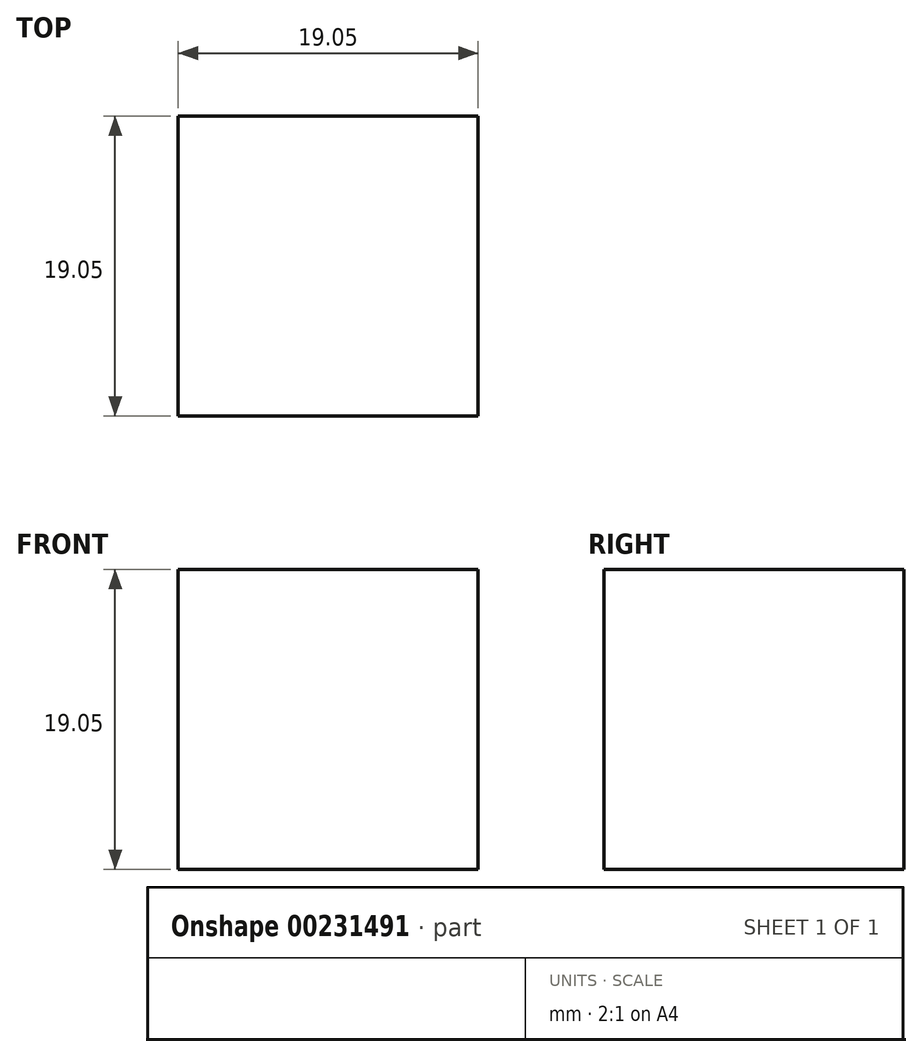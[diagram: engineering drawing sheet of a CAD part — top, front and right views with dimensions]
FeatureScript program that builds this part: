
annotation { "Feature Type Name" : "Feature", "Feature Type Description" : "" }
export const myFeature = defineFeature(function(context is Context, id is Id, definition is map)
    precondition{}
    {
        {
            var Q0;
            Q0=qCreatedBy(makeId("Front.planeOp"),FACE);
            var sketch = newSketch(context, id + "F0", { "sketchPlane" : qUnion([Q0])});
            skLineSegment(sketch, "E0.bottom", {"start": v(-64.04, 46.77) * mm, "end": v(-45, 46.77) * mm});
            skLineSegment(sketch, "E0.top", {"start": v(-64.04, 27.72) * mm, "end": v(-45, 27.72) * mm});
            skLineSegment(sketch, "E0.left", {"start": v(-64.04, 46.77) * mm, "end": v(-64.04, 27.72) * mm});
            skLineSegment(sketch, "E0.right", {"start": v(-45, 46.77) * mm, "end": v(-45, 27.72) * mm});
            skSolve(sketch);
        }
        {
            var Q0;
            Q0=makeQuery(id+"F0.imprint","IMPRINT",FACE,{"disambiguationData":[TD([[makeQuery(id+"F0.imprint","IMPRINT",EDGE,{"derivedFrom":sQuery(id+"F0.wireOp",EDGE,"E0.bottom")}),-1.0]])]});
            extrude(context, id + "F1", {"entities" : qUnion([Q0]), "depth" : 19.05 * mm});
        }
    });
